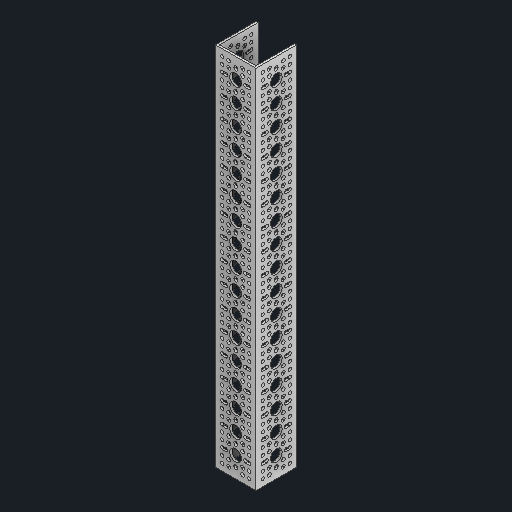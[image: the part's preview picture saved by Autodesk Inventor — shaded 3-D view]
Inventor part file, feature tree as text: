
AUTODESK INVENTOR PART (.ipt)
format: ipt  version: 2023 (Build 270158000, 158)  size: 1,744,896 bytes
history: native  units: in
note: dims shown in document units (in); Inventor stores cm internally (conversion verified against a paired STEP export)
features: mirror x1
ambient origin geometry x8: Origin, YZ Plane, XZ Plane, XY Plane, X Axis, Y Axis, Z Axis, Center Point
bodies: Solid1 (feature_tree)
feature tree (1):
  mirror  "Mirror5"
